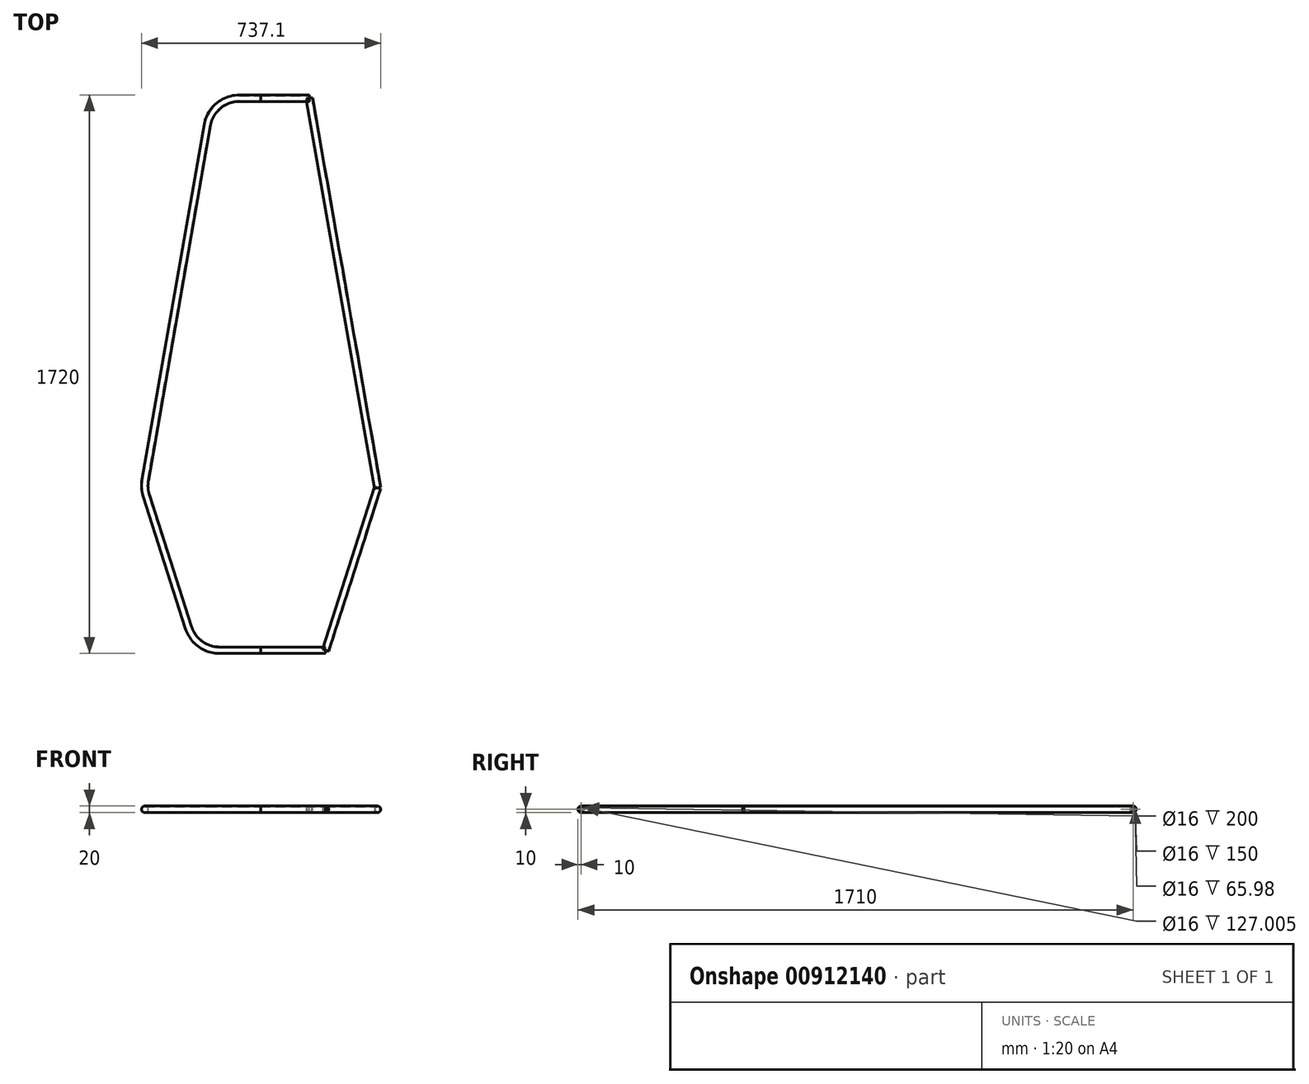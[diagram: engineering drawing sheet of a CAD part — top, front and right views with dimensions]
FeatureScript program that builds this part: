
annotation { "Feature Type Name" : "Feature", "Feature Type Description" : "" }
export const myFeature = defineFeature(function(context is Context, id is Id, definition is map)
    precondition{}
    {
        {
            var Q0;
            Q0=qCreatedBy(makeId("Top.planeOp"),FACE);
            var sketch = newSketch(context, id + "F0", { "sketchPlane" : qUnion([Q0])});
            skLineSegment(sketch, "E0", {"start": v(0, 800) * mm, "end": v(150, 800) * mm});
            skLineSegment(sketch, "E1", {"start": v(150, 800) * mm, "end": v(360, -400) * mm});
            skLineSegment(sketch, "E2", {"start": v(360, -400) * mm, "end": v(200, -900) * mm});
            skLineSegment(sketch, "E3", {"start": v(200, -900) * mm, "end": v(0, -900) * mm});
            skLineSegment(sketch, "E4.MirrorCS", {"start": v(-127, -900) * mm, "end": v(0, -900) * mm});
            skLineSegment(sketch, "E5.MirrorCS", {"start": v(0, 800) * mm, "end": v(-65.98, 800) * mm});
            skLineSegment(sketch, "E6.MirrorCS", {"start": v(-352.5, -423.46) * mm, "end": v(-222.25, -830.48) * mm});
            skLineSegment(sketch, "E7.MirrorCS", {"start": v(-164.48, 717.24) * mm, "end": v(-355.75, -375.74) * mm});
            skPoint(sketch, "E8.visualSharp", {"position": v(-360, -400) * mm});
            skArc(sketch, "E8.filletArc", {"start": v(-355.75, -375.74) * mm, "mid": v(-357.02, -399.8) * mm, "end": v(-352.5, -423.46) * mm});
            skPoint(sketch, "E9.visualSharp", {"position": v(-200, -900) * mm});
            skArc(sketch, "E9.filletArc", {"start": v(-222.25, -830.48) * mm, "mid": v(-185.96, -880.77) * mm, "end": v(-127, -900) * mm});
            skPoint(sketch, "E10.visualSharp", {"position": v(-150, 800) * mm});
            skArc(sketch, "E10.filletArc", {"start": v(-65.98, 800) * mm, "mid": v(-130.3, 776.56) * mm, "end": v(-164.48, 717.24) * mm});
            skSolve(sketch);
        }
        {
            var Q0;
            Q0=qCreatedBy(makeId("Right.planeOp"),FACE);
            var sketch = newSketch(context, id + "F1", { "sketchPlane" : qUnion([Q0])});
            skCircle(sketch, "E11", {"center": v(800, 0) * mm, "radius": 10 * mm});
            skCircle(sketch, "E12", {"center": v(800, 0) * mm, "radius": 8 * mm});
            skSolve(sketch);
        }
        {
            var Q0;
            Q0=sQuery(id+"F0.wireOp",EDGE,"E1");
            var Q1;
            Q1=sQuery(id+"F0.wireOp",VERTEX,"E1.end");
            cPlane(context, id + "F2", {"entities" : qUnion([Q0, Q1]), "cplaneType" : CPlaneType.LINE_POINT, "offset" : 25 * mm, "width" : 150 * mm, "height" : 150 * mm});
        }
        {
            var Q0;
            Q0=qCreatedBy(id+"F2.planeOp",FACE);
            var sketch = newSketch(context, id + "F3", { "sketchPlane" : qUnion([Q0])});
            skCircle(sketch, "E13", {"center": v(285.66, 0) * mm, "radius": 10 * mm});
            skCircle(sketch, "E14", {"center": v(285.66, 0) * mm, "radius": 8 * mm});
            skSolve(sketch);
        }
        {
            var Q0;
            Q0=makeQuery(id+"F3.imprint","IMPRINT",FACE,{"disambiguationData":[TD([[makeQuery(id+"F3.imprint","IMPRINT",EDGE,{"derivedFrom":sQuery(id+"F3.wireOp",EDGE,"E13")}),1.0]])]});
            var Q1;
            Q1=sQuery(id+"F3.wireOp",EDGE,"E13");
            var Q2;
            Q2=sQuery(id+"F3.wireOp",EDGE,"E14");
            var Q3;
            Q3=sQuery(id+"F0.wireOp",EDGE,"E1");
            sweep(context, id + "F4", {"profiles" : qUnion([Q0]), "surfaceProfiles" : qUnion([Q1, Q2]), "path" : qUnion([Q3])});
        }
        {
            var Q0;
            Q0=sQuery(id+"F0.wireOp",EDGE,"E2");
            var Q1;
            Q1=sQuery(id+"F0.wireOp",VERTEX,"E2.end");
            cPlane(context, id + "F5", {"entities" : qUnion([Q0, Q1]), "cplaneType" : CPlaneType.LINE_POINT, "offset" : 25 * mm, "width" : 150 * mm, "height" : 150 * mm});
        }
        {
            var Q0;
            Q0=qCreatedBy(id+"F5.planeOp",FACE);
            var sketch = newSketch(context, id + "F6", { "sketchPlane" : qUnion([Q0])});
            skCircle(sketch, "E15", {"center": v(464.78, 0) * mm, "radius": 8 * mm});
            skCircle(sketch, "E16", {"center": v(464.78, 0) * mm, "radius": 10 * mm});
            skSolve(sketch);
        }
        {
            var Q0;
            Q0=makeQuery(id+"F6.imprint","IMPRINT",FACE,{"disambiguationData":[TD([[makeQuery(id+"F6.imprint","IMPRINT",EDGE,{"derivedFrom":sQuery(id+"F6.wireOp",EDGE,"E15")}),-1.0]])]});
            var Q1;
            Q1=sQuery(id+"F0.wireOp",EDGE,"E2");
            sweep(context, id + "F7", {"profiles" : qUnion([Q0]), "path" : qUnion([Q1])});
        }
        {
            var Q0;
            Q0=sQuery(id+"F0.wireOp",VERTEX,"E3.end");
            var Q1;
            Q1=sQuery(id+"F0.wireOp",EDGE,"E3");
            cPlane(context, id + "F8", {"entities" : qUnion([Q0, Q1]), "cplaneType" : CPlaneType.LINE_POINT, "offset" : 25 * mm, "width" : 150 * mm, "height" : 150 * mm});
        }
        {
            var Q0;
            Q0=qCreatedBy(id+"F8.planeOp",FACE);
            var sketch = newSketch(context, id + "F9", { "sketchPlane" : qUnion([Q0])});
            skCircle(sketch, "E17", {"center": v(900, 0) * mm, "radius": 10 * mm});
            skCircle(sketch, "E18", {"center": v(900, 0) * mm, "radius": 8 * mm});
            skSolve(sketch);
        }
        {
            var Q0;
            Q0=makeQuery(id+"F9.imprint","IMPRINT",FACE,{"disambiguationData":[TD([[makeQuery(id+"F9.imprint","IMPRINT",EDGE,{"derivedFrom":sQuery(id+"F9.wireOp",EDGE,"E17")}),1.0]])]});
            var Q1;
            Q1=sQuery(id+"F0.wireOp",EDGE,"E3");
            sweep(context, id + "F10", {"profiles" : qUnion([Q0]), "path" : qUnion([Q1])});
        }
        {
            var Q0;
            Q0=makeQuery(id+"F1.imprint","IMPRINT",FACE,{"disambiguationData":[TD([[makeQuery(id+"F1.imprint","IMPRINT",EDGE,{"derivedFrom":sQuery(id+"F1.wireOp",EDGE,"E11")}),1.0]])]});
            var Q1;
            Q1=sQuery(id+"F0.wireOp",EDGE,"E0");
            sweep(context, id + "F11", {"profiles" : qUnion([Q0]), "path" : qUnion([Q1])});
        }
        {
            var Q0;
            Q0=makeQuery(id+"F10.opSweep","CAP_FACE",FACE,{"disambiguationData":[OSD([sQuery(id+"F0.wireOp",VERTEX,"E3.end"),sQuery(id+"F9.wireOp",EDGE,"E17"),sQuery(id+"F9.wireOp",EDGE,"E18")])],"isStart":true});
            var Q1;
            Q1=sQuery(id+"F0.wireOp",EDGE,"E4.MirrorCS");
            var Q2;
            Q2=sQuery(id+"F0.wireOp",EDGE,"E9.filletArc");
            var Q3;
            Q3=sQuery(id+"F0.wireOp",EDGE,"E6.MirrorCS");
            var Q4;
            Q4=sQuery(id+"F0.wireOp",EDGE,"E8.filletArc");
            var Q5;
            Q5=sQuery(id+"F0.wireOp",EDGE,"E7.MirrorCS");
            var Q6;
            Q6=sQuery(id+"F0.wireOp",EDGE,"E10.filletArc");
            var Q7;
            Q7=sQuery(id+"F0.wireOp",EDGE,"E5.MirrorCS");
            sweep(context, id + "F12", {"profiles" : qUnion([Q0]), "path" : qUnion([Q1, Q2, Q3, Q4, Q5, Q6, Q7])});
        }
    });
